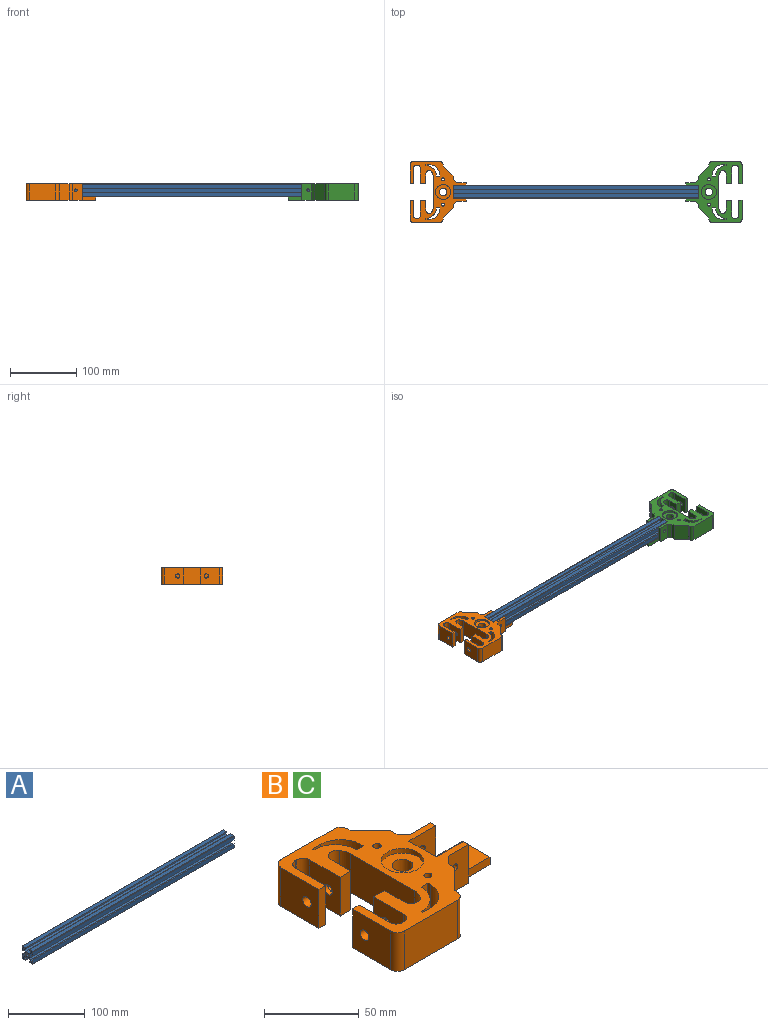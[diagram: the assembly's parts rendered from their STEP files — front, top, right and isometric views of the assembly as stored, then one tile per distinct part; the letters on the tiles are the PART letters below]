
ASSEMBLY  parts=3 mates=6
PART A: 51 faces, bbox 370x20x20 mm
  f0: plane 370x2mm, normal (0,-1,0), area 740mm2, adj f1,f48,f49,f50
  f1: plane 370x3mm, normal (0,0,-1), area 1110mm2, adj f0,f2,f49,f50
  f2: plane 370x1mm, normal (0,-1,0), area 370mm2, adj f1,f3,f49,f50
  f3: plane 370x3mm, normal (0,-0.71,0.71), area 1569.8mm2, adj f2,f4,f49,f50
  f4: plane 370x6mm, normal (0,0,1), area 2220mm2, adj f3,f5,f49,f50
  f5: plane 370x3mm, normal (0,0.71,0.71), area 1569.8mm2, adj f4,f6,f49,f50
  f6: plane 370x1mm, normal (0,1,0), area 370mm2, adj f5,f7,f49,f50
  f7: plane 370x3mm, normal (0,0,-1), area 1110mm2, adj f6,f8,f49,f50
  f8: plane 370x2mm, normal (0,1,0), area 740mm2, adj f7,f9,f49,f50
  f9: plane 370x6mm, normal (0,0,1), area 2220mm2, adj f8,f10,f49,f50
  f10: cylinder r=1mm len=370mm, axis (-1,0,0), area 581.2mm2, adj f9,f11,f49,f50
  f11: plane 370x6mm, normal (0,-1,0), area 2220mm2, adj f10,f12,f49,f50
  f12: plane 370x2mm, normal (0,0,-1), area 740mm2, adj f11,f13,f49,f50
  f13: plane 370x3mm, normal (0,1,0), area 1110mm2, adj f12,f14,f49,f50
  f14: plane 370x1mm, normal (0,0,-1), area 370mm2, adj f13,f15,f49,f50
  f15: plane 370x3mm, normal (0,-0.71,-0.71), area 1569.8mm2, adj f14,f16,f49,f50
  f16: plane 370x6mm, normal (0,-1,0), area 2220mm2, adj f15,f17,f49,f50
  f17: plane 370x3mm, normal (0,-0.71,0.71), area 1569.8mm2, adj f16,f18,f49,f50
  f18: plane 370x1mm, normal (0,0,1), area 370mm2, adj f17,f19,f49,f50
  f19: plane 370x3mm, normal (0,1,0), area 1110mm2, adj f18,f20,f49,f50
  f20: plane 370x2mm, normal (0,0,1), area 740mm2, adj f19,f21,f49,f50
  f21: plane 370x6mm, normal (0,-1,0), area 2220mm2, adj f20,f22,f49,f50
  f22: cylinder r=1mm len=370mm, axis (-1,0,0), area 581.2mm2, adj f21,f23,f49,f50
  f23: plane 370x6mm, normal (0,0,-1), area 2220mm2, adj f22,f24,f49,f50
  f24: plane 370x2mm, normal (0,1,0), area 740mm2, adj f23,f25,f49,f50
  f25: plane 370x3mm, normal (0,0,1), area 1110mm2, adj f24,f26,f49,f50
  f26: plane 370x1mm, normal (0,1,0), area 370mm2, adj f25,f27,f49,f50
  f27: plane 370x3mm, normal (0,0.71,-0.71), area 1569.8mm2, adj f26,f28,f49,f50
  f28: plane 370x6mm, normal (0,0,-1), area 2220mm2, adj f27,f29,f49,f50
  f29: plane 370x3mm, normal (0,-0.71,-0.71), area 1569.8mm2, adj f28,f30,f49,f50
  f30: plane 370x1mm, normal (0,-1,0), area 370mm2, adj f29,f31,f49,f50
  f31: plane 370x3mm, normal (0,0,1), area 1110mm2, adj f30,f32,f49,f50
  f32: plane 370x2mm, normal (0,-1,0), area 740mm2, adj f31,f33,f49,f50
  f33: plane 370x6mm, normal (0,0,-1), area 2220mm2, adj f32,f34,f49,f50
  f34: cylinder r=1mm len=370mm, axis (-1,0,0), area 581.2mm2, adj f33,f35,f49,f50
  f35: plane 370x6mm, normal (0,1,0), area 2220mm2, adj f34,f36,f49,f50
  f36: plane 370x2mm, normal (0,0,1), area 740mm2, adj f35,f37,f49,f50
  f37: plane 370x3mm, normal (0,-1,0), area 1110mm2, adj f36,f38,f49,f50
  f38: plane 370x1mm, normal (0,0,1), area 370mm2, adj f37,f39,f49,f50
  f39: plane 370x3mm, normal (0,0.71,0.71), area 1569.8mm2, adj f38,f40,f49,f50
  f40: plane 370x6mm, normal (0,1,0), area 2220mm2, adj f39,f41,f49,f50
  f41: plane 370x3mm, normal (0,0.71,-0.71), area 1569.8mm2, adj f40,f42,f49,f50
  f42: plane 370x1mm, normal (0,0,-1), area 370mm2, adj f41,f43,f49,f50
  f43: plane 370x3mm, normal (0,-1,0), area 1110mm2, adj f42,f44,f49,f50
  f44: plane 370x2mm, normal (0,0,-1), area 740mm2, adj f43,f45,f49,f50
  f45: plane 370x6mm, normal (0,1,0), area 2220mm2, adj f44,f46,f49,f50
  f46: cylinder r=1mm len=370mm, axis (-1,0,0), area 581.2mm2, adj f45,f48,f49,f50
  f47: cylinder r=2.1mm len=370mm, axis (-1,0,0), area 4882mm2, adj f49,f50
  f48: plane 370x6mm, normal (0,0,1), area 2220mm2, adj f0,f46,f49,f50
  f49: plane 20x20mm, normal (1,0,0), area 181.3mm2, adj f0,f1,f2,f3,f4,f5,f6,f7
  f50: plane 20x20mm, normal (-1,0,0), area 181.3mm2, adj f0,f1,f2,f3,f4,f5,f6,f7
PART B: 113 faces, bbox 104.8x92x25 mm
  f0: plane 25x14.82mm, normal (1,0,0), area 302.8mm2, adj f5,f15,f77,f92,f93,f94,f95,f96
  f1: cylinder r=3.12mm len=6.25mm, axis (-1,0,0), area 58.9mm2, adj f76,f98
  f2: cylinder r=3.12mm len=6.25mm, axis (-1,0,0), area 58.9mm2, adj f65,f85
  f3: plane 25x5mm, normal (0,1,0), area 125mm2, adj f5,f15,f79,f82
  f4: plane 25x5mm, normal (0,-1,0), area 125mm2, adj f5,f15,f58,f61
  f5: plane 104.75x92mm, normal (0,0,-1), area 4255mm2, adj f0,f3,f4,f6,f7,f8,f12,f13
  f6: plane 25x15mm, normal (0,-1,0), area 360.8mm2, adj f5,f8,f15,f19,f55
  f7: cylinder r=5.5mm len=22mm, axis (0,0,-1), area 760.3mm2, adj f5,f17
  f8: plane 25x3.75mm, normal (1,0,0), area 93.8mm2, adj f5,f6,f9,f15,f21
  f9: plane 20x20mm, normal (0,1,0), area 385.8mm2, adj f8,f10,f15,f19,f25
  f10: plane 20.5x20mm, normal (1,0,0), area 410mm2, adj f9,f11,f15,f25
  f11: plane 20x20mm, normal (0,-1,0), area 385.8mm2, adj f10,f12,f15,f18,f25
  f12: plane 25x3.75mm, normal (1,0,0), area 93.8mm2, adj f5,f11,f13,f15,f20
  f13: plane 25x15mm, normal (0,1,0), area 360.8mm2, adj f5,f12,f15,f18,f54
  f14: plane 48x25mm, normal (-1,0,0), area 1200mm2, adj f5,f15,f62,f78
  f15: plane 92x84.75mm, normal (0,0,1), area 3194.9mm2, adj f0,f3,f4,f6,f8,f9,f10,f11
  f16: cylinder r=11.2mm len=22.4mm, axis (0,0,1), area 211.1mm2, adj f15,f17
  f17: plane 22.4x22.4mm, normal (0,0,1), area 299mm2, adj f7,f16
  f18: cylinder r=2.12mm len=4.25mm, axis (0,-1,0), area 50.1mm2, adj f11,f13
  f19: cylinder r=2.12mm len=4.25mm, axis (0,-1,0), area 50.1mm2, adj f6,f9
  f20: plane 20x5mm, normal (0,1,0), area 100mm2, adj f5,f12,f24,f25
  f21: plane 20x5mm, normal (0,-1,0), area 100mm2, adj f5,f8,f24,f25
  f22: cylinder r=2.12mm len=5mm, axis (0,0,-1), area 66.8mm2, adj f5,f25
  f23: cylinder r=2.12mm len=5mm, axis (0,0,-1), area 66.8mm2, adj f5,f25
  f24: plane 20.5x5mm, normal (1,0,0), area 102.5mm2, adj f5,f20,f21,f25
  f25: plane 40x20.5mm, normal (0,0,1), area 791.6mm2, adj f9,f10,f11,f20,f21,f22,f23,f24
  f26: plane 25x5mm, normal (1,0,0), area 125mm2, adj f5,f15,f54,f99
  f27: cylinder r=2.12mm len=5.71mm, axis (0,0,-1), area 74.9mm2, adj f15,f42,f43,f44,f45,f46,f47
  f28: plane 25x5mm, normal (1,0,0), area 125mm2, adj f5,f15,f55,f100
  f29: cylinder r=2.12mm len=5.71mm, axis (0,0,-1), area 74.9mm2, adj f15,f48,f49,f50,f51,f52,f53
  f30: plane 18.5x3.37mm, normal (0,1,0), area 62.3mm2, adj f5,f31,f35,f48
  f31: plane 18.5x2.92mm, normal (-0.87,0.5,0), area 62.3mm2, adj f5,f30,f32,f50
  f32: plane 18.5x2.92mm, normal (-0.87,-0.5,0), area 62.3mm2, adj f5,f31,f33,f52
  f33: plane 18.5x3.37mm, normal (0,-1,0), area 62.3mm2, adj f5,f32,f34,f53
  f34: plane 18.5x2.92mm, normal (0.87,-0.5,0), area 62.3mm2, adj f5,f33,f35,f51
  f35: plane 18.5x2.92mm, normal (0.87,0.5,0), area 62.3mm2, adj f5,f30,f34,f49
  f36: plane 18.5x2.92mm, normal (-0.87,-0.5,0), area 62.3mm2, adj f5,f37,f41,f47
  f37: plane 18.5x3.37mm, normal (0,-1,0), area 62.3mm2, adj f5,f36,f38,f46
  f38: plane 18.5x2.92mm, normal (0.87,-0.5,0), area 62.3mm2, adj f5,f37,f39,f44
  f39: plane 18.5x2.92mm, normal (0.87,0.5,0), area 62.3mm2, adj f5,f38,f40,f42
  f40: plane 18.5x3.37mm, normal (0,1,0), area 62.3mm2, adj f5,f39,f41,f43
  f41: plane 18.5x2.92mm, normal (-0.87,0.5,0), area 62.3mm2, adj f5,f36,f40,f45
  f42: plane 2.92x2.31mm, normal (0.61,0.35,-0.71), area 3.6mm2, adj f27,f39,f43,f44
  f43: plane 3.37x1.08mm, normal (0,0.71,-0.71), area 3.6mm2, adj f27,f40,f42,f45
  f44: plane 2.92x2.31mm, normal (0.61,-0.35,-0.71), area 3.6mm2, adj f27,f38,f42,f46
  f45: plane 2.92x2.31mm, normal (-0.61,0.35,-0.71), area 3.6mm2, adj f27,f41,f43,f47
  f46: plane 3.37x1.08mm, normal (0,-0.71,-0.71), area 3.6mm2, adj f27,f37,f44,f47
  f47: plane 2.92x2.31mm, normal (-0.61,-0.35,-0.71), area 3.6mm2, adj f27,f36,f45,f46
  f48: plane 3.37x1.08mm, normal (0,0.71,-0.71), area 3.6mm2, adj f29,f30,f49,f50
  f49: plane 2.92x2.31mm, normal (0.61,0.35,-0.71), area 3.6mm2, adj f29,f35,f48,f51
  f50: plane 2.92x2.31mm, normal (-0.61,0.35,-0.71), area 3.6mm2, adj f29,f31,f48,f52
  f51: plane 2.92x2.31mm, normal (0.61,-0.35,-0.71), area 3.6mm2, adj f29,f34,f49,f53
  f52: plane 2.92x2.31mm, normal (-0.61,-0.35,-0.71), area 3.6mm2, adj f29,f32,f50,f53
  f53: plane 3.37x1.08mm, normal (0,-0.71,-0.71), area 3.6mm2, adj f29,f33,f51,f52
  f54: plane 25x5mm, normal (0.71,0.71,0), area 176.8mm2, adj f5,f13,f15,f26
  f55: plane 25x5mm, normal (0.71,-0.71,0), area 176.8mm2, adj f5,f6,f15,f28
  f56: plane 39.75x25mm, normal (0,-1,0), area 993.8mm2, adj f5,f15,f105,f106
  f57: plane 25x2mm, normal (1,0,0), area 50mm2, adj f5,f15,f100,f105
  f58: plane 25x2mm, normal (-1,0,0), area 50mm2, adj f4,f5,f15,f102
  f59: plane 25x6mm, normal (0,1,0), area 150mm2, adj f5,f15,f60,f102
  f60: plane 25x1mm, normal (1,0,0), area 25mm2, adj f5,f15,f59,f61
  f61: cylinder r=16mm len=25mm, axis (0,0,-1), area 628.3mm2, adj f4,f5,f15,f60
  f62: cylinder r=11mm len=25mm, axis (0,0,-1), area 161.1mm2, adj f5,f14,f15,f110
  f63: plane 25x14.82mm, normal (1,0,0), area 302.8mm2, adj f5,f15,f64,f86,f87,f88,f89,f90
  f64: plane 25x8mm, normal (0,1,0), area 200mm2, adj f5,f15,f63,f65
  f65: plane 25x22.5mm, normal (-1,0,0), area 531.8mm2, adj f2,f5,f15,f64,f111
  f66: plane 25x0.75mm, normal (0,1,0), area 18.8mm2, adj f5,f15,f111,f112
  f67: plane 25x22.5mm, normal (1,0,0), area 531.8mm2, adj f5,f15,f68,f84,f112
  f68: plane 25x5mm, normal (0,1,0), area 125mm2, adj f5,f15,f67,f69
  f69: plane 28.5x25mm, normal (-1,0,0), area 681.8mm2, adj f5,f15,f68,f84,f106
  f70: plane 25x2mm, normal (1,0,0), area 50mm2, adj f5,f15,f99,f103
  f71: plane 39.75x25mm, normal (0,1,0), area 993.8mm2, adj f5,f15,f103,f104
  f72: plane 28.5x25mm, normal (-1,0,0), area 681.8mm2, adj f5,f15,f73,f83,f104
  f73: plane 25x5mm, normal (0,-1,0), area 125mm2, adj f5,f15,f72,f74
  f74: plane 25x22.5mm, normal (1,0,0), area 531.8mm2, adj f5,f15,f73,f83,f107
  f75: plane 25x0.75mm, normal (0,-1,0), area 18.8mm2, adj f5,f15,f107,f108
  f76: plane 25x22.5mm, normal (-1,0,0), area 531.8mm2, adj f1,f5,f15,f77,f108
  f77: plane 25x8mm, normal (0,-1,0), area 200mm2, adj f0,f5,f15,f76
  f78: cylinder r=11mm len=25mm, axis (0,0,-1), area 161.1mm2, adj f5,f14,f15,f109
  f79: cylinder r=16mm len=25mm, axis (0,0,-1), area 628.3mm2, adj f3,f5,f15,f80
  f80: plane 25x1mm, normal (1,0,0), area 25mm2, adj f5,f15,f79,f81
  f81: plane 25x6mm, normal (0,-1,0), area 150mm2, adj f5,f15,f80,f101
  f82: plane 25x2mm, normal (-1,0,0), area 50mm2, adj f3,f5,f15,f101
  f83: cylinder r=3.12mm len=6.25mm, axis (-1,0,0), area 98.2mm2, adj f72,f74
  f84: cylinder r=3.12mm len=6.25mm, axis (-1,0,0), area 98.2mm2, adj f67,f69
  f85: plane 10.2x8.84mm, normal (1,0,0), area 36.9mm2, adj f2,f86,f87,f88,f89,f90,f91
  f86: plane 5x4.42mm, normal (0,-0.5,0.87), area 25.5mm2, adj f63,f85,f87,f91
  f87: plane 5.1x5mm, normal (0,-1,0), area 25.5mm2, adj f63,f85,f86,f88
  f88: plane 5x4.42mm, normal (0,-0.5,-0.87), area 25.5mm2, adj f63,f85,f87,f89
  f89: plane 5x4.42mm, normal (0,0.5,-0.87), area 25.5mm2, adj f63,f85,f88,f90
  f90: plane 5.1x5mm, normal (0,1,0), area 25.5mm2, adj f63,f85,f89,f91
  f91: plane 5x4.42mm, normal (0,0.5,0.87), area 25.5mm2, adj f63,f85,f86,f90
  f92: plane 5x4.42mm, normal (0,-0.5,0.87), area 25.5mm2, adj f0,f93,f97,f98
  f93: plane 5.1x5mm, normal (0,-1,0), area 25.5mm2, adj f0,f92,f94,f98
  f94: plane 5x4.42mm, normal (0,-0.5,-0.87), area 25.5mm2, adj f0,f93,f95,f98
  f95: plane 5x4.42mm, normal (0,0.5,-0.87), area 25.5mm2, adj f0,f94,f96,f98
  f96: plane 5.1x5mm, normal (0,1,0), area 25.5mm2, adj f0,f95,f97,f98
  f97: plane 5x4.42mm, normal (0,0.5,0.87), area 25.5mm2, adj f0,f92,f96,f98
  f98: plane 10.2x8.84mm, normal (1,0,0), area 36.9mm2, adj f1,f92,f93,f94,f95,f96,f97
  f99: plane 25x15mm, normal (0.71,0.71,0), area 530.3mm2, adj f5,f15,f26,f70
  f100: plane 25x15mm, normal (0.71,-0.71,0), area 530.3mm2, adj f5,f15,f28,f57
  f101: cylinder r=15mm len=25mm, axis (0,0,1), area 589mm2, adj f5,f15,f81,f82
  f102: cylinder r=15mm len=25mm, axis (0,0,1), area 589mm2, adj f5,f15,f58,f59
  f103: cylinder r=5mm len=25mm, axis (0,0,-1), area 196.3mm2, adj f5,f15,f70,f71
  f104: cylinder r=5mm len=25mm, axis (0,0,-1), area 196.3mm2, adj f5,f15,f71,f72
  f105: cylinder r=5mm len=25mm, axis (0,0,-1), area 196.3mm2, adj f5,f15,f56,f57
  f106: cylinder r=5mm len=25mm, axis (0,0,-1), area 196.3mm2, adj f5,f15,f56,f69
  f107: cylinder r=5mm len=25mm, axis (0,0,-1), area 196.3mm2, adj f5,f15,f74,f75
  f108: cylinder r=5mm len=25mm, axis (0,0,1), area 196.3mm2, adj f5,f15,f75,f76
  f109: cylinder r=5mm len=25mm, axis (0,0,-1), area 319.5mm2, adj f0,f5,f15,f78
  f110: cylinder r=5mm len=25mm, axis (0,0,-1), area 319.5mm2, adj f5,f15,f62,f63
  f111: cylinder r=5mm len=25mm, axis (0,0,1), area 196.3mm2, adj f5,f15,f65,f66
  f112: cylinder r=5mm len=25mm, axis (0,0,-1), area 196.3mm2, adj f5,f15,f66,f67
PART C: same geometry as B
PLACE A t=(-8.29,-0.01,0.11)mm fixed
PLACE B t=(-208.29,-0.26,-14.89)mm
PLACE C rot(axis=(0,0,1),180deg) t=(191.71,-0.26,-14.89)mm
MATE planar B.f10 <-> A.f50  axis (1,0,0) through (-193.29,-0.26,0.11)mm
MATE planar B.f11 <-> A.f45  axis (0,-1,0) through (-183.29,9.99,10.11)mm
MATE planar A.f33 <-> B.f25  axis (0,0,-1) through (-8.29,5.99,-9.89)mm
MATE planar C.f10 <-> A.f47  axis (-1,0,0) through (176.71,-0.26,0.11)mm
MATE planar C.f18 <-> A.f35  axis (0,-1,0) through (166.71,9.99,0.11)mm
MATE planar C.f5 <-> B.f5  axis (0,0,-1) through (194.88,-0.26,-14.89)mm
